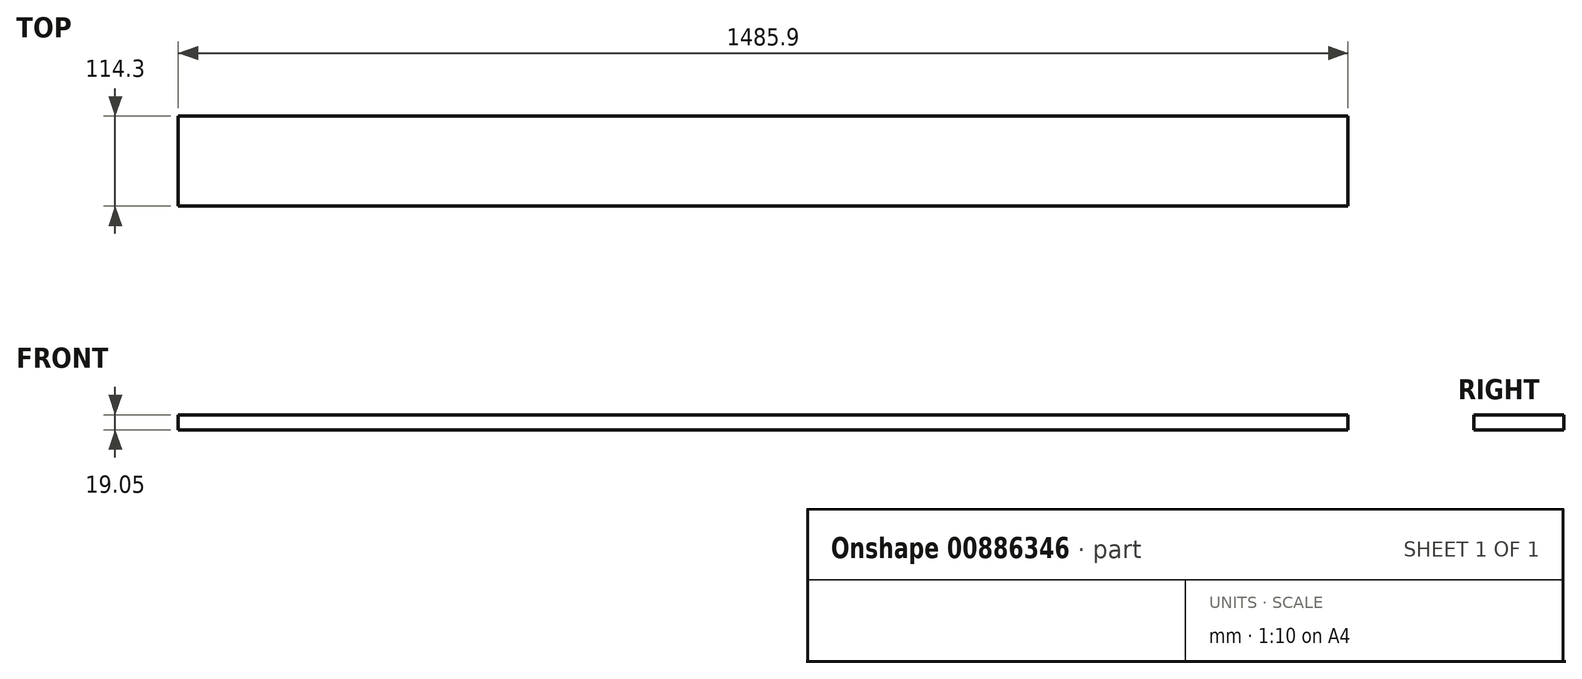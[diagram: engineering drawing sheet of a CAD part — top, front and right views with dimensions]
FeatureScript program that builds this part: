
annotation { "Feature Type Name" : "Feature", "Feature Type Description" : "" }
export const myFeature = defineFeature(function(context is Context, id is Id, definition is map)
    precondition{}
    {
        {
            var Q0;
            Q0=qCreatedBy(makeId("Top.planeOp"),FACE);
            var sketch = newSketch(context, id + "F0", { "sketchPlane" : qUnion([Q0])});
            skLineSegment(sketch, "E0.bottom", {"start": v(-742.95, 57.15) * mm, "end": v(742.95, 57.15) * mm});
            skLineSegment(sketch, "E0.top", {"start": v(-742.95, -57.15) * mm, "end": v(742.95, -57.15) * mm});
            skLineSegment(sketch, "E0.left", {"start": v(-742.95, 57.15) * mm, "end": v(-742.95, -57.15) * mm});
            skLineSegment(sketch, "E0.right", {"start": v(742.95, 57.15) * mm, "end": v(742.95, -57.15) * mm});
            skPoint(sketch, "E0.middle", {"position": v(0, 0) * mm});
            skSolve(sketch);
        }
        {
            var Q0;
            Q0=makeQuery(id+"F0.imprint","IMPRINT",FACE,{"disambiguationData":[TD([[makeQuery(id+"F0.imprint","IMPRINT",EDGE,{"derivedFrom":sQuery(id+"F0.wireOp",EDGE,"E0.bottom")}),-1.0]])]});
            extrude(context, id + "F1", {"entities" : qUnion([Q0]), "depth" : 19.05 * mm, "offsetDistance" : 25.4 * mm});
        }
    });
